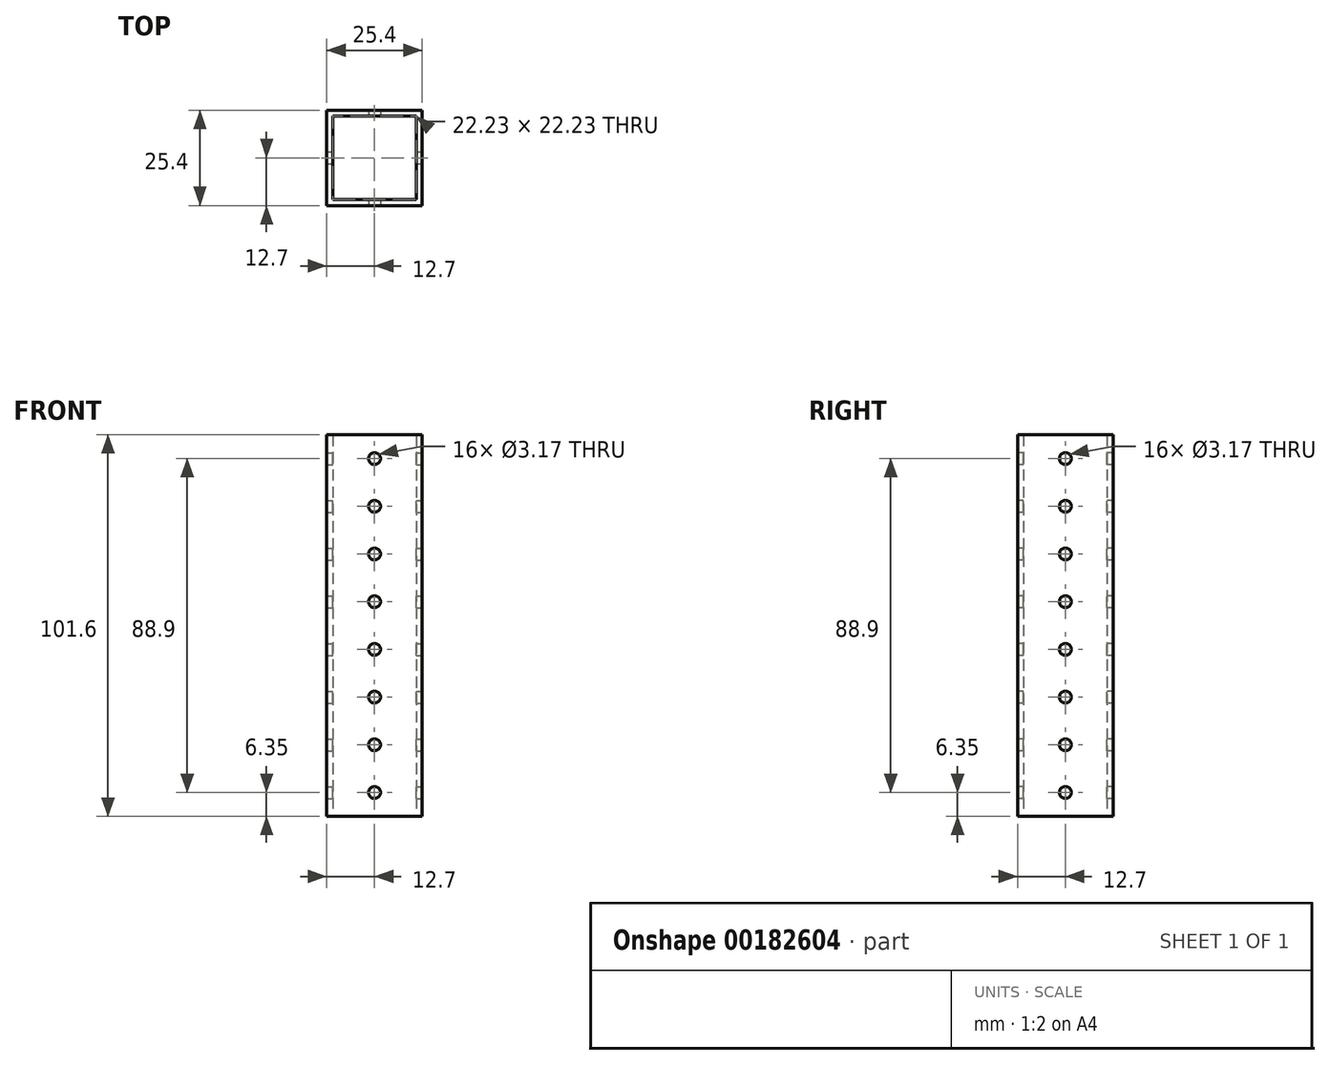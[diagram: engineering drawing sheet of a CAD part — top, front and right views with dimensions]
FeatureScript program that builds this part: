
annotation { "Feature Type Name" : "Feature", "Feature Type Description" : "" }
export const myFeature = defineFeature(function(context is Context, id is Id, definition is map)
    precondition{}
    {
        {
            var Q0;
            Q0=qCreatedBy(makeId("Top.planeOp"),FACE);
            var sketch = newSketch(context, id + "F0", { "sketchPlane" : qUnion([Q0])});
            skLineSegment(sketch, "E0.bottom", {"start": v(12.7, 12.7) * mm, "end": v(-12.7, 12.7) * mm});
            skLineSegment(sketch, "E0.top", {"start": v(12.7, -12.7) * mm, "end": v(-12.7, -12.7) * mm});
            skLineSegment(sketch, "E0.left", {"start": v(12.7, 12.7) * mm, "end": v(12.7, -12.7) * mm});
            skLineSegment(sketch, "E0.right", {"start": v(-12.7, 12.7) * mm, "end": v(-12.7, -12.7) * mm});
            skPoint(sketch, "E0.middle", {"position": v(0, 0) * mm});
            skLineSegment(sketch, "E1.bottom", {"start": v(11.11, 11.11) * mm, "end": v(-11.11, 11.11) * mm});
            skLineSegment(sketch, "E1.top", {"start": v(11.11, -11.11) * mm, "end": v(-11.11, -11.11) * mm});
            skLineSegment(sketch, "E1.left", {"start": v(11.11, 11.11) * mm, "end": v(11.11, -11.11) * mm});
            skLineSegment(sketch, "E1.right", {"start": v(-11.11, 11.11) * mm, "end": v(-11.11, -11.11) * mm});
            skSolve(sketch);
        }
        {
            var Q0;
            Q0 = qSketchRegion(id + "F0", true);
            extrude(context, id + "F1", {"entities" : qUnion([Q0]), "depth" : 101.6 * mm});
        }
        {
            var Q0;
            Q0=makeQuery(id+"F1.opExtrude","SWEPT_FACE",FACE,{"disambiguationData":[OSD([sQuery(id+"F0.wireOp",EDGE,"E0.top")])]});
            var sketch = newSketch(context, id + "F2", { "sketchPlane" : qUnion([Q0])});
            skLineSegment(sketch, "E2", {"start": v(0, 101.6) * mm, "end": v(0, 0) * mm});
            skCircle(sketch, "E3", {"center": v(0, 6.35) * mm, "radius": 1.59 * mm});
            skCircle(sketch, "E4", {"center": v(0, 19.05) * mm, "radius": 1.59 * mm});
            skCircle(sketch, "E5", {"center": v(0, 31.75) * mm, "radius": 1.59 * mm});
            skCircle(sketch, "E6", {"center": v(0, 44.45) * mm, "radius": 1.59 * mm});
            skLineSegment(sketch, "E7", {"start": v(-12.7, 50.8) * mm, "end": v(12.7, 50.8) * mm});
            skCircle(sketch, "E8.MirrorC", {"center": v(0, 57.15) * mm, "radius": 1.59 * mm});
            skCircle(sketch, "E9.MirrorC", {"center": v(0, 69.85) * mm, "radius": 1.59 * mm});
            skCircle(sketch, "E10.MirrorC", {"center": v(0, 82.55) * mm, "radius": 1.59 * mm});
            skCircle(sketch, "E11.MirrorC", {"center": v(0, 95.25) * mm, "radius": 1.59 * mm});
            skCircle(sketch, "E12.3.0.0", {"center": v(92.64, -11) * mm, "radius": 1.59 * mm});
            skCircle(sketch, "E12.4.0.0", {"center": v(123.52, -46.43) * mm, "radius": 1.59 * mm});
            skSolve(sketch);
        }
        {
            var Q0;
            Q0 = qSketchRegion(id + "F2", true);
            extrude(context, id + "F3", {"entities" : qUnion([Q0]), "operationType" : NewBodyOperationType.REMOVE, "oppositeDirection" : true, "depth" : 25.4 * mm});
        }
        {
            var Q0;
            Q0=makeQuery(id+"F1.opExtrude","SWEPT_FACE",FACE,{"disambiguationData":[OSD([sQuery(id+"F0.wireOp",EDGE,"E0.left")])]});
            var sketch = newSketch(context, id + "F4", { "sketchPlane" : qUnion([Q0])});
            skLineSegment(sketch, "E13", {"start": v(0, 101.6) * mm, "end": v(0, 0) * mm});
            skLineSegment(sketch, "E14", {"start": v(-12.7, 50.8) * mm, "end": v(12.7, 50.8) * mm});
            skCircle(sketch, "E15", {"center": v(0, 6.35) * mm, "radius": 1.59 * mm});
            skCircle(sketch, "E16", {"center": v(0, 19.05) * mm, "radius": 1.59 * mm});
            skCircle(sketch, "E17", {"center": v(0, 31.75) * mm, "radius": 1.59 * mm});
            skCircle(sketch, "E18", {"center": v(0, 44.45) * mm, "radius": 1.59 * mm});
            skPoint(sketch, "E19", {"position": v(0, 50.8) * mm});
            skCircle(sketch, "E20.MirrorC", {"center": v(0, 57.15) * mm, "radius": 1.59 * mm});
            skCircle(sketch, "E21.MirrorC", {"center": v(0, 69.85) * mm, "radius": 1.59 * mm});
            skCircle(sketch, "E22.MirrorC", {"center": v(0, 82.55) * mm, "radius": 1.59 * mm});
            skCircle(sketch, "E23.MirrorC", {"center": v(0, 95.25) * mm, "radius": 1.59 * mm});
            skSolve(sketch);
        }
        {
            var Q0;
            Q0 = qSketchRegion(id + "F4", true);
            extrude(context, id + "F5", {"entities" : qUnion([Q0]), "operationType" : NewBodyOperationType.REMOVE, "oppositeDirection" : true, "depth" : 25.4 * mm});
        }
    });
